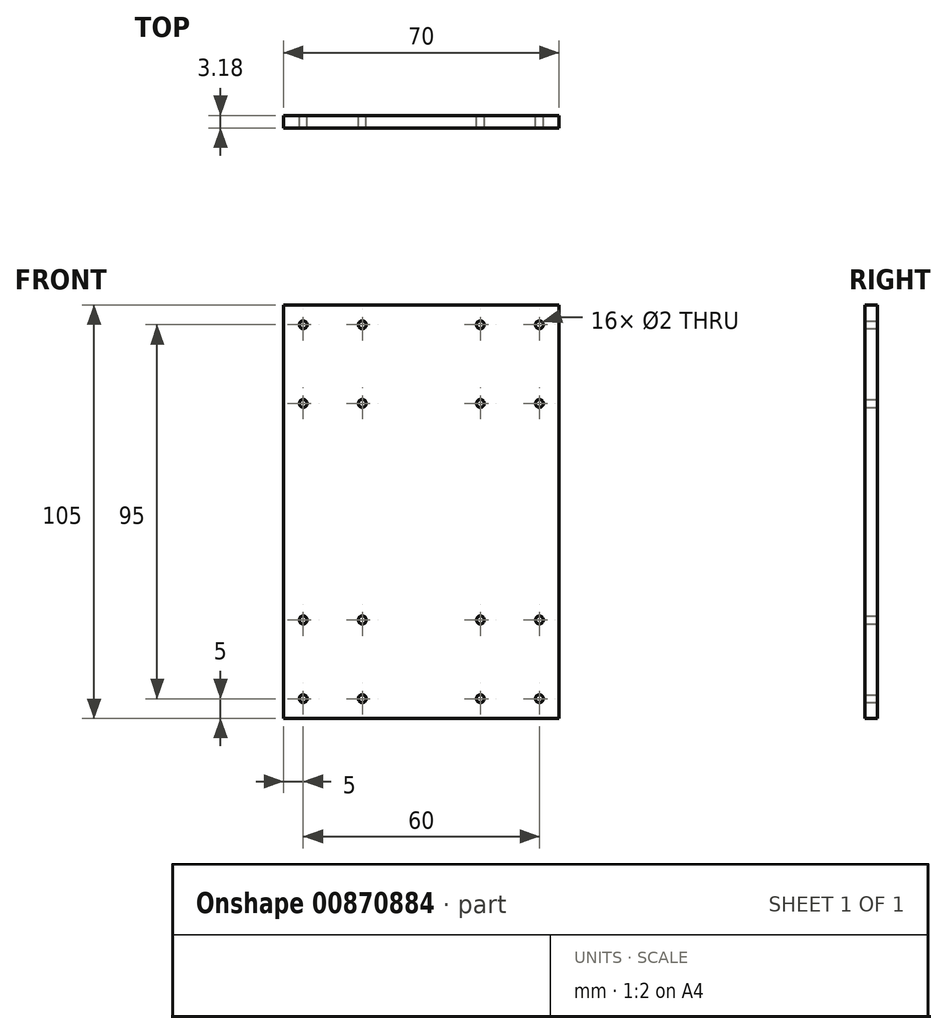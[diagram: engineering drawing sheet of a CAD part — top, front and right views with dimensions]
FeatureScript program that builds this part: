
annotation { "Feature Type Name" : "Feature", "Feature Type Description" : "" }
export const myFeature = defineFeature(function(context is Context, id is Id, definition is map)
    precondition{}
    {
        {
            var Q0;
            Q0=qCreatedBy(makeId("Front.planeOp"),FACE);
            var sketch = newSketch(context, id + "F0", { "sketchPlane" : qUnion([Q0])});
            skLineSegment(sketch, "E0.bottom", {"start": v(35, 52.5) * mm, "end": v(-35, 52.5) * mm});
            skLineSegment(sketch, "E0.top", {"start": v(35, -52.5) * mm, "end": v(-35, -52.5) * mm});
            skLineSegment(sketch, "E0.left", {"start": v(35, 52.5) * mm, "end": v(35, -52.5) * mm});
            skLineSegment(sketch, "E0.right", {"start": v(-35, 52.5) * mm, "end": v(-35, -52.5) * mm});
            skPoint(sketch, "E0.middle", {"position": v(0, 0) * mm});
            skPoint(sketch, "E1", {"position": v(-30, 47.5) * mm});
            skPoint(sketch, "E2", {"position": v(-15, 27.5) * mm});
            skPoint(sketch, "E3", {"position": v(-30, 27.5) * mm});
            skPoint(sketch, "E4", {"position": v(-15, 47.5) * mm});
            skPoint(sketch, "E5", {"position": v(15, 47.5) * mm});
            skPoint(sketch, "E6", {"position": v(30, 47.5) * mm});
            skPoint(sketch, "E7", {"position": v(30, 27.5) * mm});
            skPoint(sketch, "E8", {"position": v(15, 27.5) * mm});
            skPoint(sketch, "E9", {"position": v(15, -27.5) * mm});
            skPoint(sketch, "E10", {"position": v(30, -27.5) * mm});
            skPoint(sketch, "E11", {"position": v(30, -47.5) * mm});
            skPoint(sketch, "E12", {"position": v(15, -47.5) * mm});
            skPoint(sketch, "E13", {"position": v(-15, -47.5) * mm});
            skPoint(sketch, "E14", {"position": v(-15, -27.5) * mm});
            skPoint(sketch, "E15", {"position": v(-30, -27.5) * mm});
            skPoint(sketch, "E16", {"position": v(-30, -47.5) * mm});
            skCircle(sketch, "E17", {"center": v(-30, 47.5) * mm, "radius": 1 * mm});
            skCircle(sketch, "E18", {"center": v(-15, 47.5) * mm, "radius": 1 * mm});
            skCircle(sketch, "E19", {"center": v(-15, 27.5) * mm, "radius": 1 * mm});
            skCircle(sketch, "E20", {"center": v(-30, 27.5) * mm, "radius": 1 * mm});
            skCircle(sketch, "E21", {"center": v(15, 47.5) * mm, "radius": 1 * mm});
            skCircle(sketch, "E22", {"center": v(30, 47.5) * mm, "radius": 1 * mm});
            skCircle(sketch, "E23", {"center": v(30, 27.5) * mm, "radius": 1 * mm});
            skCircle(sketch, "E24", {"center": v(15, 27.5) * mm, "radius": 1 * mm});
            skCircle(sketch, "E25", {"center": v(15, -27.5) * mm, "radius": 1 * mm});
            skCircle(sketch, "E26", {"center": v(30, -27.5) * mm, "radius": 1 * mm});
            skCircle(sketch, "E27", {"center": v(15, -47.5) * mm, "radius": 1 * mm});
            skCircle(sketch, "E28", {"center": v(30, -47.5) * mm, "radius": 1 * mm});
            skCircle(sketch, "E29", {"center": v(-15, -47.5) * mm, "radius": 1 * mm});
            skCircle(sketch, "E30", {"center": v(-15, -27.5) * mm, "radius": 1 * mm});
            skCircle(sketch, "E31", {"center": v(-30, -27.5) * mm, "radius": 1 * mm});
            skCircle(sketch, "E32", {"center": v(-30, -47.5) * mm, "radius": 1 * mm});
            skSolve(sketch);
        }
        {
            var Q0;
            Q0 = qSketchRegion(id + "F0", true);
            extrude(context, id + "F1", {"entities" : qUnion([Q0]), "depth" : 3.17 * mm, "offsetDistance" : 25 * mm});
        }
    });
